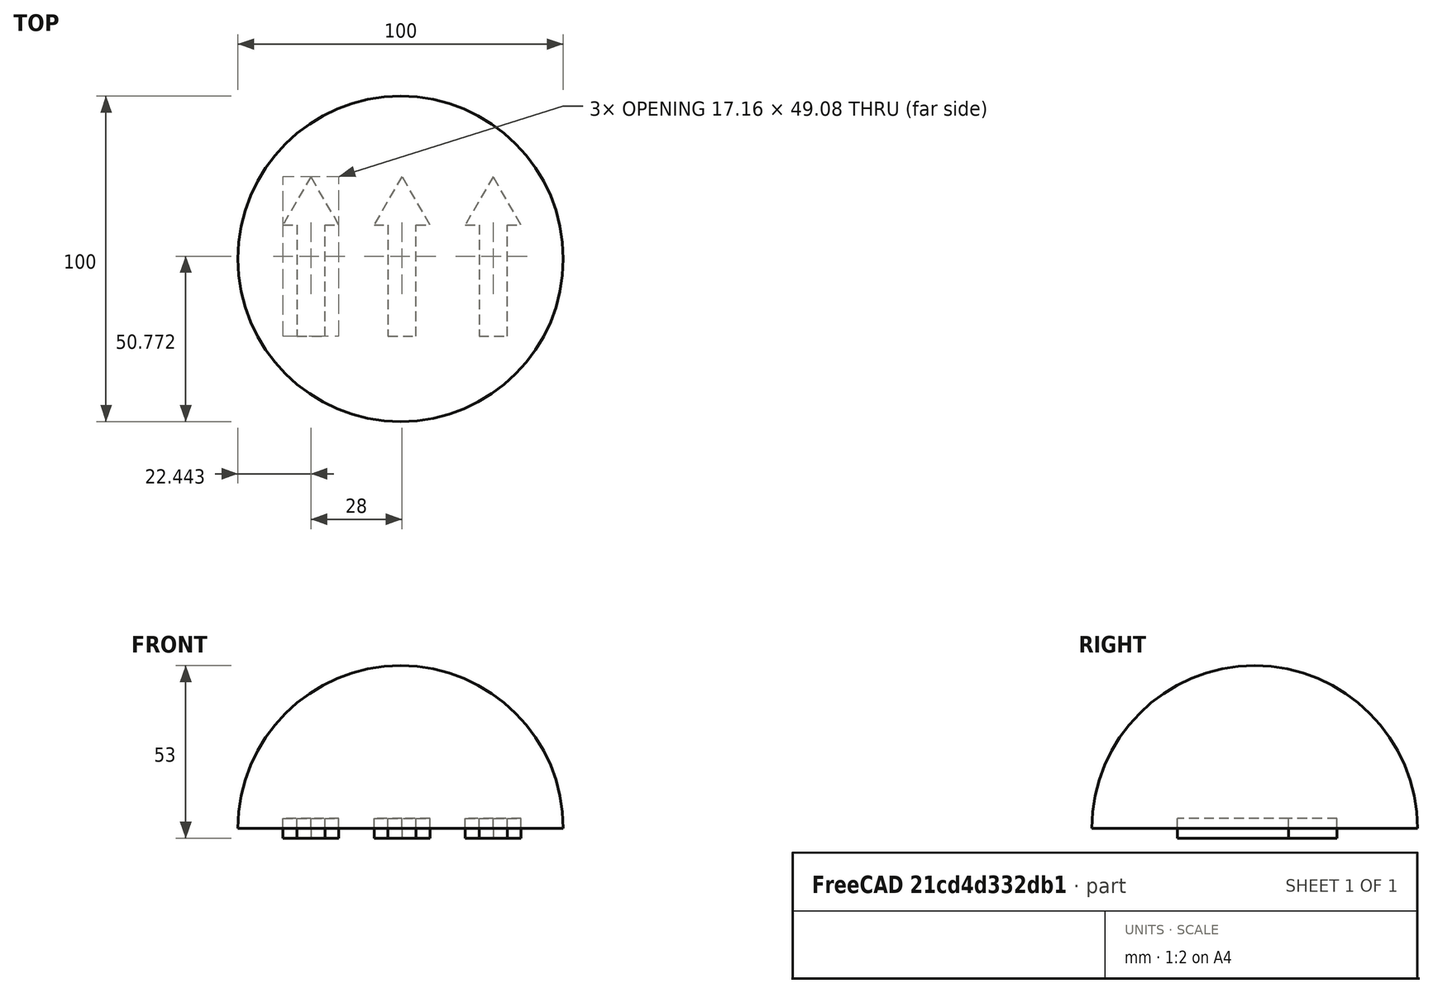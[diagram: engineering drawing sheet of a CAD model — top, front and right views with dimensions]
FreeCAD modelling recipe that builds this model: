
FCSTD DOCUMENT  (FreeCAD 0.15R4671 (Git))
Label: magnetized_sphere
License: All rights reserved
LicenseURL: http://en.wikipedia.org/wiki/All_rights_reserved
objects: Part::Extrusion×11, Part::Part2DObjectPython×8, Part::Feature×6, Part::Cut×5, Part::Sphere×2, Mesh::Feature×2, Part::MultiFuse×1
note: 33 computed .brp shape members not serialized (recipe doc carries the construction recipe); baked Part::Feature solids carry a one-line shape summary decoded from their .brp

FEATURE [Part::Sphere] Sphere
  Angle1 = -90
  Angle2 = 90
  Angle3 = 360
  Radius = 50
FEATURE [Part::Part2DObjectPython] Rectangle  # Draft 2D object (typed FeaturePython)
  ChamferSize = 0
  FilletRadius = 0
  Height = -100
  Length = 100
  MakeFace = true
  Placement = pos=(-50,50,0) rot=(0,0,1;0rad)
FEATURE [Part::Extrusion] Extrude
  Base = -> Rectangle
  Dir = (0,0,-50)
  Solid = false
FEATURE [Part::Cut] Cut
  Base = -> Sphere
  Tool = -> Extrude
FEATURE [Part::Feature] Face
  shape: bbox 8.605 x 34.58 x 2e-07 mm, 1 faces, 0 solids (baked)
FEATURE [Part::Feature] Face001
  shape: bbox 17.16 x 14.86 x 2e-07 mm, 1 faces, 0 solids (baked)
FEATURE [Part::Part2DObjectPython] Fusion  # Draft 2D object (typed FeaturePython)
  Base = -> Face
  ChamferSize = 0
  Closed = false
  End = (4.7456,10.4534,0)
  FilletRadius = 0
  Length = 0
  MakeFace = true
  Placement = pos=(-17,30,0) rot=(0,0,1;0rad)
  Points = (7) [(26.0236,-19.5466,0),(17.4435,-4.68592,0),(8.86199,-19.5466,0),(13.1405,-19.5466,0),(13.1405,-53.7696,0),(21.7456,-53.7696,0),(21.7456,-19.5466,0)]
  Start = (9.02364,10.4534,0)
  Tool = -> Face001
FEATURE [Part::Feature] Face002
  shape: bbox 8.605 x 34.58 x 2e-07 mm, 1 faces, 0 solids (baked)
FEATURE [Part::Feature] Face003
  shape: bbox 17.16 x 14.86 x 2e-07 mm, 1 faces, 0 solids (baked)
FEATURE [Part::Part2DObjectPython] Fusion001  # Draft 2D object (typed FeaturePython)
  Base = -> Face002
  ChamferSize = 0
  Closed = false
  End = (-23.2544,10.4534,0)
  FilletRadius = 0
  Length = 0
  MakeFace = true
  Placement = pos=(-45,30,0) rot=(0,0,1;0rad)
  Points = (7) [(26.0236,-19.5466,0),(17.4435,-4.68592,0),(8.86199,-19.5466,0),(13.1405,-19.5466,0),(13.1405,-53.7696,0),(21.7456,-53.7696,0),(21.7456,-19.5466,0)]
  Start = (-18.9764,10.4534,0)
  Tool = -> Face003
FEATURE [Part::Feature] Face004
  shape: bbox 8.605 x 34.58 x 2e-07 mm, 1 faces, 0 solids (baked)
FEATURE [Part::Feature] Face005
  shape: bbox 17.16 x 14.86 x 2e-07 mm, 1 faces, 0 solids (baked)
FEATURE [Part::Part2DObjectPython] Fusion002  # Draft 2D object (typed FeaturePython)
  Base = -> Face004
  ChamferSize = 0
  Closed = false
  End = (32.7456,10.4534,0)
  FilletRadius = 0
  Length = 0
  MakeFace = true
  Placement = pos=(11,30,0) rot=(0,0,1;0rad)
  Points = (7) [(26.0236,-19.5466,0),(17.4435,-4.68592,0),(8.86199,-19.5466,0),(13.1405,-19.5466,0),(13.1405,-53.7696,0),(21.7456,-53.7696,0),(21.7456,-19.5466,0)]
  Start = (37.0236,10.4534,0)
  Tool = -> Face005
FEATURE [Part::Part2DObjectPython] Clone2D  label="Clone of Fusion (2D)"  # Draft 2D object (typed FeaturePython)
  Objects = -> [Fusion]
  Placement = pos=(-17,30,0) rot=(0,0,1;0rad)
  Scale = (0.8,0.8,1)
FEATURE [Part::Part2DObjectPython] Clone2D001  label="Clone of Fusion001 (2D)"  # Draft 2D object (typed FeaturePython)
  Objects = -> [Fusion001]
  Placement = pos=(-45,30,0) rot=(0,0,1;0rad)
  Scale = (0.8,0.8,1)
FEATURE [Part::Part2DObjectPython] Clone2D002  label="Clone of Fusion002 (2D)"  # Draft 2D object (typed FeaturePython)
  Objects = -> [Fusion002]
  Placement = pos=(11,30,0) rot=(0,0,1;0rad)
  Scale = (0.8,0.8,1)
FEATURE [Part::Extrusion] Extrude001
  Base = -> Fusion
  Dir = (0,0,3)
  Solid = false
FEATURE [Part::Extrusion] Extrude002
  Base = -> Fusion001
  Dir = (0,0,3)
  Solid = false
FEATURE [Part::Extrusion] Extrude003
  Base = -> Fusion002
  Dir = (0,0,3)
  Solid = false
FEATURE [Part::Sphere] Sphere001
  Angle1 = -90
  Angle2 = 90
  Angle3 = 360
  Radius = 50
FEATURE [Part::Part2DObjectPython] Rectangle001  # Draft 2D object (typed FeaturePython)
  ChamferSize = 0
  FilletRadius = 0
  Height = -100
  Length = 100
  MakeFace = true
  Placement = pos=(-50,50,0) rot=(0,0,1;0rad)
FEATURE [Part::Extrusion] Extrude004
  Base = -> Rectangle001
  Dir = (0,0,-50)
  Solid = false
FEATURE [Part::Cut] Cut001
  Base = -> Sphere001
  Tool = -> Extrude004
FEATURE [Part::Cut] Cut002
  Base = -> Cut
  Tool = -> Extrude001
FEATURE [Part::Cut] Cut003
  Base = -> Cut002
  Tool = -> Extrude003
FEATURE [Part::Cut] Cut004  label="counter bored magnetization"
  Base = -> Cut003
  Tool = -> Extrude002
FEATURE [Part::Extrusion] Extrude005
  Base = -> Clone2D
  Dir = (0,0,-3)
  Solid = false
FEATURE [Part::Extrusion] Extrude006
  Base = -> Clone2D001
  Dir = (0,0,-3)
  Solid = false
FEATURE [Part::Extrusion] Extrude007
  Base = -> Clone2D002
  Dir = (0,0,-3)
  Solid = false
FEATURE [Part::Extrusion] Extrude008
  Base = -> Clone2D
  Dir = (0,0,-3)
  Solid = false
FEATURE [Part::Extrusion] Extrude009
  Base = -> Clone2D001
  Dir = (0,0,-3)
  Solid = false
FEATURE [Part::Extrusion] Extrude010
  Base = -> Clone2D002
  Dir = (0,0,-3)
  Solid = false
FEATURE [Part::MultiFuse] Fusion003  label="extruded magnetization"
  Shapes = -> [Extrude007,Extrude005,Extrude006,Cut001]
FEATURE [Mesh::Feature] Mesh  label="counter bored magnetization (Meshed)"
FEATURE [Mesh::Feature] Mesh001  label="extruded magnetization (Meshed)"
